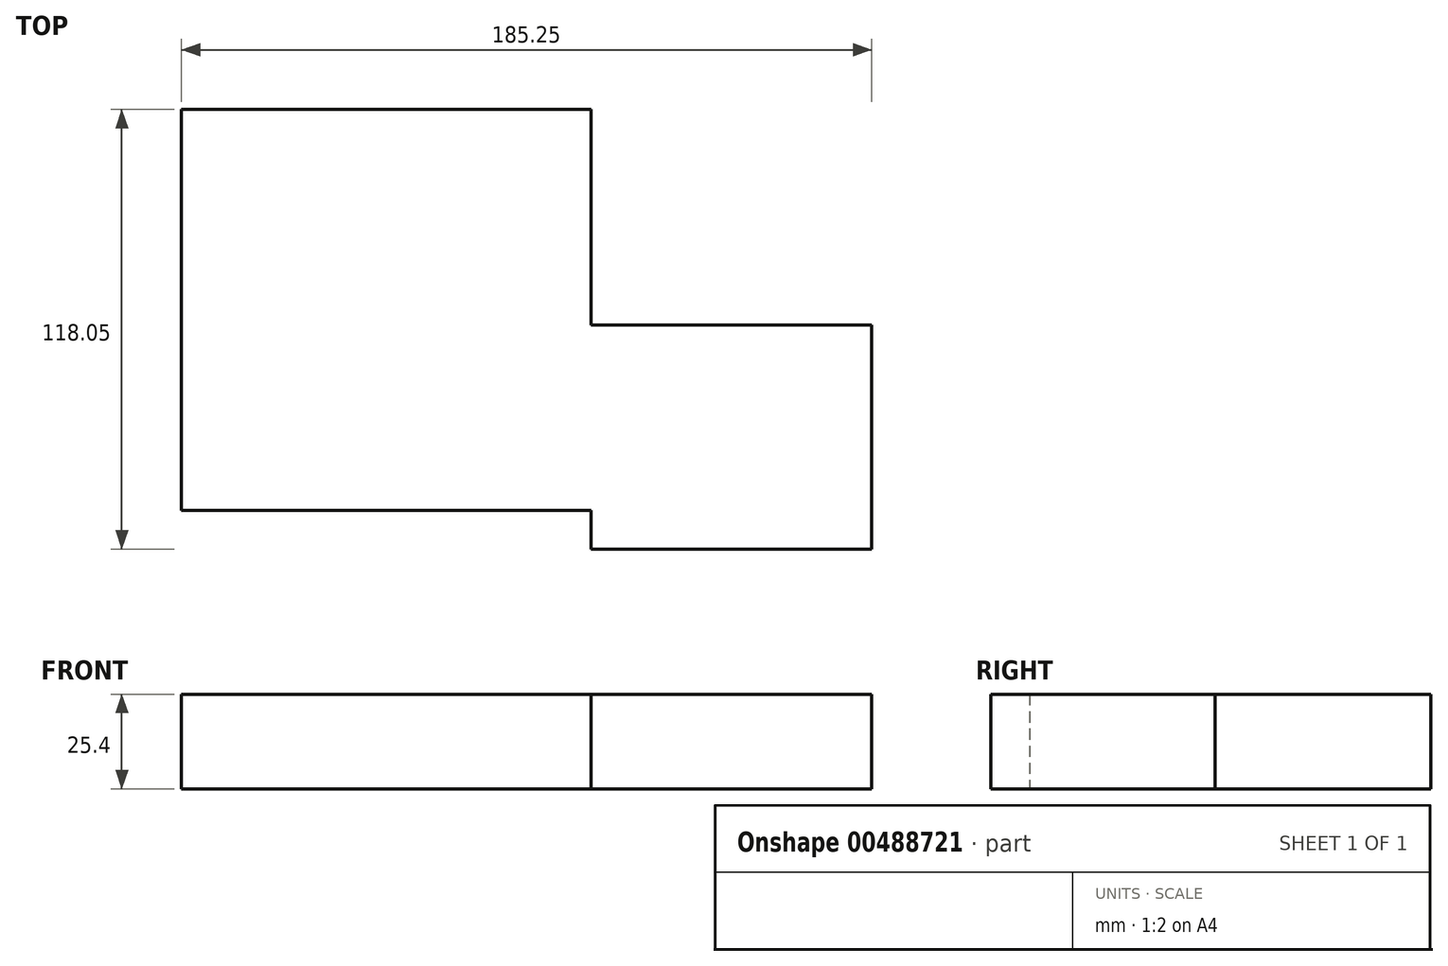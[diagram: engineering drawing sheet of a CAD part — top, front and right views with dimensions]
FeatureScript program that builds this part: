
annotation { "Feature Type Name" : "Feature", "Feature Type Description" : "" }
export const myFeature = defineFeature(function(context is Context, id is Id, definition is map)
    precondition{}
    {
        {
            var Q0;
            Q0=qCreatedBy(makeId("Top.planeOp"),FACE);
            var sketch = newSketch(context, id + "F0", { "sketchPlane" : qUnion([Q0])});
            skLineSegment(sketch, "E0.bottom", {"start": v(54.97, -53.82) * mm, "end": v(-54.97, -53.82) * mm});
            skLineSegment(sketch, "E0.top", {"start": v(54.97, 53.82) * mm, "end": v(-54.97, 53.82) * mm});
            skLineSegment(sketch, "E0.left", {"start": v(54.97, -53.82) * mm, "end": v(54.97, 53.82) * mm});
            skLineSegment(sketch, "E0.right", {"start": v(-54.97, -53.82) * mm, "end": v(-54.97, 53.82) * mm});
            skPoint(sketch, "E0.middle", {"position": v(0, 0) * mm});
            skLineSegment(sketch, "E1.bottom", {"start": v(54.97, -64.23) * mm, "end": v(54.97, -64.23) * mm});
            skLineSegment(sketch, "E1.top", {"start": v(54.97, -7.34) * mm, "end": v(54.97, -7.34) * mm});
            skLineSegment(sketch, "E1.left", {"start": v(54.97, -64.23) * mm, "end": v(54.97, -7.34) * mm});
            skLineSegment(sketch, "E1.right", {"start": v(54.97, -64.23) * mm, "end": v(54.97, -7.34) * mm});
            skPoint(sketch, "E1.middle", {"position": v(54.97, -35.78) * mm});
            skLineSegment(sketch, "E2.bottom", {"start": v(54.97, -64.23) * mm, "end": v(130.28, -64.23) * mm});
            skLineSegment(sketch, "E2.top", {"start": v(54.97, -4.08) * mm, "end": v(130.28, -4.08) * mm});
            skLineSegment(sketch, "E2.left", {"start": v(54.97, -64.23) * mm, "end": v(54.97, -4.08) * mm});
            skLineSegment(sketch, "E2.right", {"start": v(130.28, -64.23) * mm, "end": v(130.28, -4.08) * mm});
            skPoint(sketch, "E2.middle", {"position": v(92.63, -34.15) * mm});
            skSolve(sketch);
        }
        {
            var Q0;
            Q0 = qSketchRegion(id + "F0", true);
            extrude(context, id + "F1", {"entities" : qUnion([Q0]), "depth" : 25.4 * mm});
        }
    });
